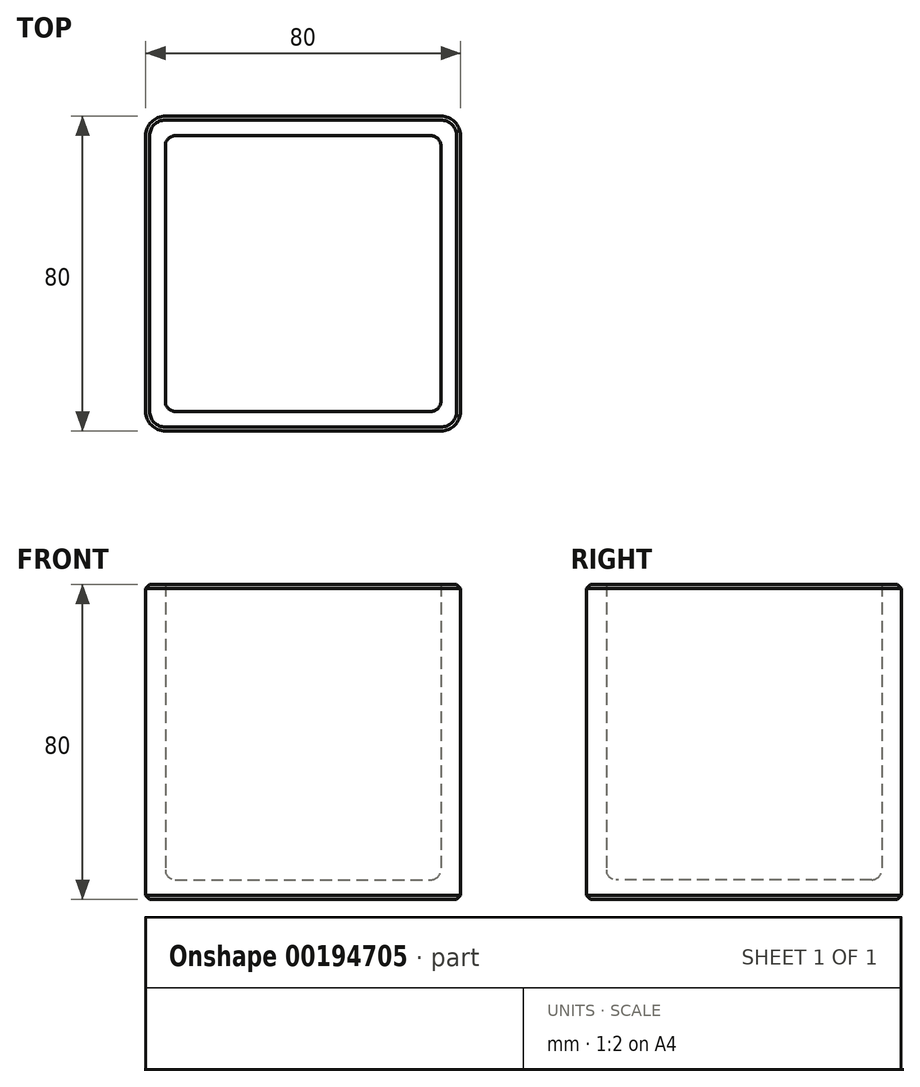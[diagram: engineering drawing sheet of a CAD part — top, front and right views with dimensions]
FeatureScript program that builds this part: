
annotation { "Feature Type Name" : "Feature", "Feature Type Description" : "" }
export const myFeature = defineFeature(function(context is Context, id is Id, definition is map)
    precondition{}
    {
        {
            var Q0;
            Q0=qCreatedBy(makeId("Top.planeOp"),FACE);
            var sketch = newSketch(context, id + "F0", { "sketchPlane" : qUnion([Q0])});
            skLineSegment(sketch, "E0.bottom", {"start": v(-35, 40) * mm, "end": v(35, 40) * mm});
            skLineSegment(sketch, "E0.top", {"start": v(-35, -40) * mm, "end": v(35, -40) * mm});
            skLineSegment(sketch, "E0.left", {"start": v(-40, 35) * mm, "end": v(-40, -35) * mm});
            skLineSegment(sketch, "E0.right", {"start": v(40, 35) * mm, "end": v(40, -35) * mm});
            skPoint(sketch, "E0.middle", {"position": v(0, 0) * mm});
            skPoint(sketch, "E1.visualSharp", {"position": v(-40, 40) * mm});
            skArc(sketch, "E1.filletArc", {"start": v(-35, 40) * mm, "mid": v(-38.54, 38.54) * mm, "end": v(-40, 35) * mm});
            skPoint(sketch, "E2.visualSharp", {"position": v(40, 40) * mm});
            skArc(sketch, "E2.filletArc", {"start": v(40, 35) * mm, "mid": v(38.54, 38.54) * mm, "end": v(35, 40) * mm});
            skPoint(sketch, "E3.visualSharp", {"position": v(40, -40) * mm});
            skArc(sketch, "E3.filletArc", {"start": v(35, -40) * mm, "mid": v(38.54, -38.54) * mm, "end": v(40, -35) * mm});
            skPoint(sketch, "E4.visualSharp", {"position": v(-40, -40) * mm});
            skArc(sketch, "E4.filletArc", {"start": v(-40, -35) * mm, "mid": v(-38.54, -38.54) * mm, "end": v(-35, -40) * mm});
            skSolve(sketch);
        }
        {
            var Q0;
            Q0=makeQuery(id+"F0.imprint","IMPRINT",FACE,{"disambiguationData":[TD([[makeQuery(id+"F0.imprint","IMPRINT",EDGE,{"derivedFrom":sQuery(id+"F0.wireOp",EDGE,"E0.bottom")}),-1.0]])]});
            extrude(context, id + "F1", {"entities" : qUnion([Q0]), "depth" : 80 * mm});
        }
        {
            var Q0;
            Q0=makeQuery(id+"F1.opExtrude","CAP_FACE",FACE,{"disambiguationData":[OSD([sQuery(id+"F0.wireOp",EDGE,"E0.bottom"),sQuery(id+"F0.wireOp",EDGE,"E0.top"),sQuery(id+"F0.wireOp",EDGE,"E0.left"),sQuery(id+"F0.wireOp",EDGE,"E0.right"),sQuery(id+"F0.wireOp",EDGE,"E1.filletArc"),sQuery(id+"F0.wireOp",EDGE,"E2.filletArc"),sQuery(id+"F0.wireOp",EDGE,"E3.filletArc"),sQuery(id+"F0.wireOp",EDGE,"E4.filletArc")])],"isStart":false});
            shell(context, id + "F2", {"entities" : qUnion([Q0]), "thickness" : 5 * mm});
        }
        {
            var Q0;
            Q0=makeQuery(id+"F2.opShell","OFFSET_EDGE",EDGE,{"disambiguationData":[OSD([sQuery(id+"F0.wireOp",EDGE,"E0.bottom"),sQuery(id+"F0.wireOp",EDGE,"E0.right"),sQuery(id+"F0.wireOp",EDGE,"E2.filletArc")])]});
            var Q1;
            Q1=makeQuery(id+"F2.opShell","OFFSET_EDGE",EDGE,{"disambiguationData":[OSD([sQuery(id+"F0.wireOp",EDGE,"E0.bottom"),sQuery(id+"F0.wireOp",EDGE,"E0.left"),sQuery(id+"F0.wireOp",EDGE,"E1.filletArc")])]});
            var Q2;
            Q2=makeQuery(id+"F2.opShell","OFFSET_EDGE",EDGE,{"disambiguationData":[OSD([sQuery(id+"F0.wireOp",EDGE,"E0.top"),sQuery(id+"F0.wireOp",EDGE,"E0.left"),sQuery(id+"F0.wireOp",EDGE,"E4.filletArc")])]});
            var Q3;
            Q3=makeQuery(id+"F2.opShell","OFFSET_EDGE",EDGE,{"disambiguationData":[OSD([sQuery(id+"F0.wireOp",EDGE,"E0.top"),sQuery(id+"F0.wireOp",EDGE,"E0.right"),sQuery(id+"F0.wireOp",EDGE,"E3.filletArc")])]});
            var Q4;
            Q4=makeQuery(id+"F2.opShell","OFFSET_FACE",FACE,{"disambiguationData":[OSD([sQuery(id+"F0.wireOp",EDGE,"E0.bottom"),sQuery(id+"F0.wireOp",EDGE,"E0.top"),sQuery(id+"F0.wireOp",EDGE,"E0.left"),sQuery(id+"F0.wireOp",EDGE,"E0.right"),sQuery(id+"F0.wireOp",EDGE,"E1.filletArc"),sQuery(id+"F0.wireOp",EDGE,"E2.filletArc"),sQuery(id+"F0.wireOp",EDGE,"E3.filletArc"),sQuery(id+"F0.wireOp",EDGE,"E4.filletArc")])]});
            fillet(context, id + "F3", {"entities" : qUnion([Q0, Q1, Q2, Q3, Q4]), "radius" : 2.5 * mm, "tangentPropagation" : true, "allowEdgeOverflow" : false});
        }
        {
            var Q0;
            Q0=makeQuery(id+"F1.opExtrude","CAP_FACE",FACE,{"disambiguationData":[OSD([sQuery(id+"F0.wireOp",EDGE,"E0.bottom"),sQuery(id+"F0.wireOp",EDGE,"E0.top"),sQuery(id+"F0.wireOp",EDGE,"E0.left"),sQuery(id+"F0.wireOp",EDGE,"E0.right"),sQuery(id+"F0.wireOp",EDGE,"E1.filletArc"),sQuery(id+"F0.wireOp",EDGE,"E2.filletArc"),sQuery(id+"F0.wireOp",EDGE,"E3.filletArc"),sQuery(id+"F0.wireOp",EDGE,"E4.filletArc")])],"isStart":true});
            var Q1;
            Q1=makeQuery(id+"F1.opExtrude","CAP_EDGE",EDGE,{"disambiguationData":[OSD([sQuery(id+"F0.wireOp",EDGE,"E0.bottom")])],"isStart":false});
            var Q2;
            Q2=makeQuery(id+"F1.opExtrude","CAP_EDGE",EDGE,{"disambiguationData":[OSD([sQuery(id+"F0.wireOp",EDGE,"E1.filletArc")])],"isStart":false});
            chamfer(context, id + "F4", {"entities" : qUnion([Q0, Q1, Q2]), "width" : 1 * mm, "tangentPropagation" : true});
        }
    });
